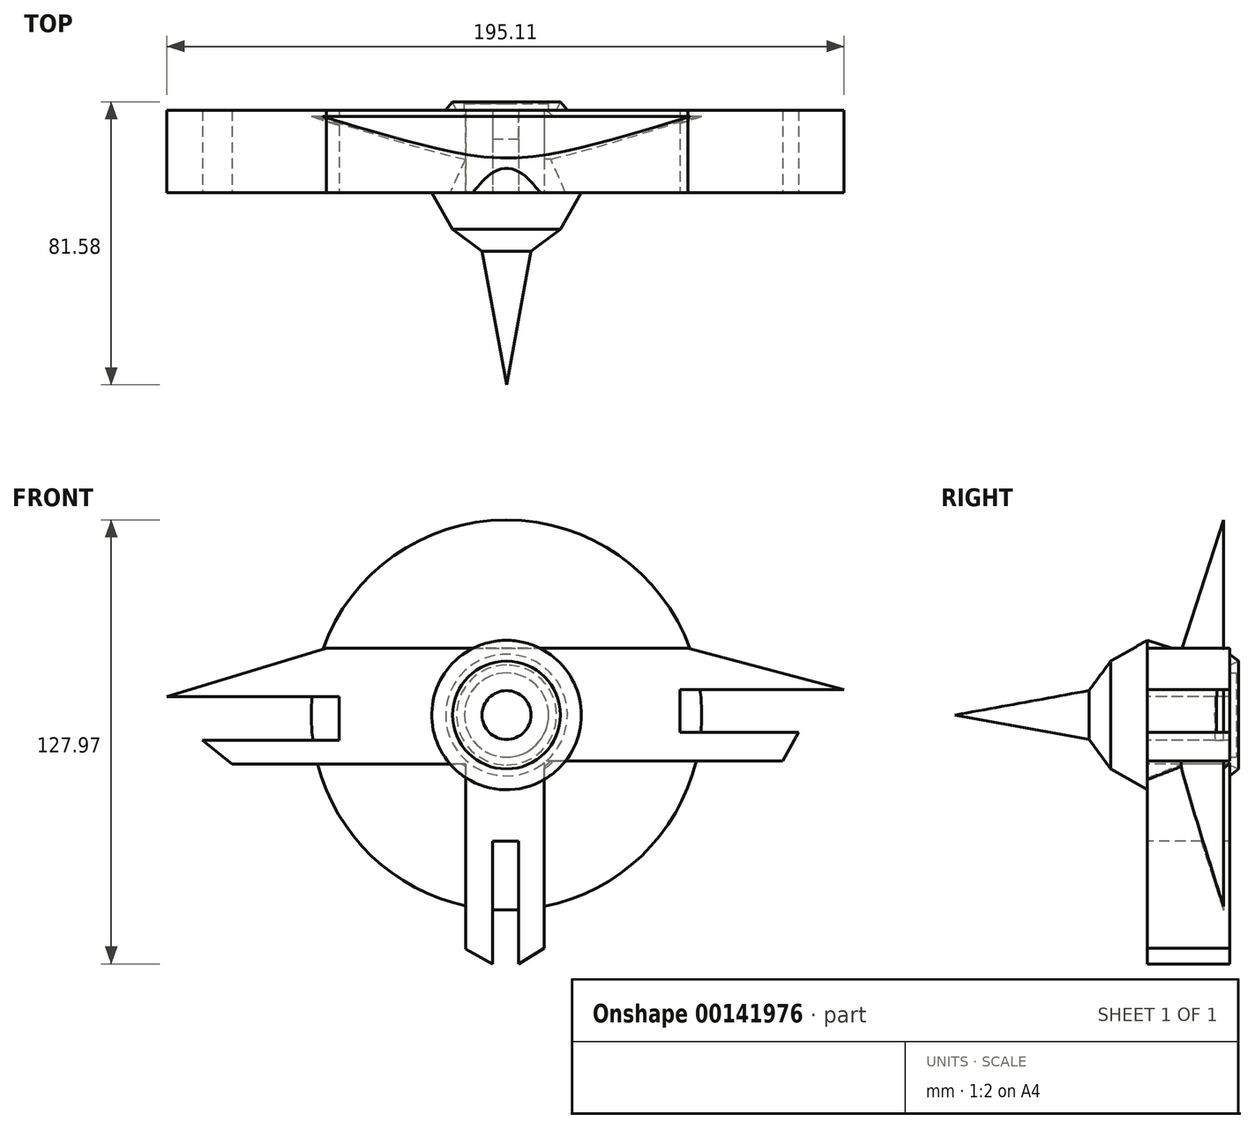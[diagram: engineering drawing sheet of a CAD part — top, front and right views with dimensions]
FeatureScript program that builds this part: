
annotation { "Feature Type Name" : "Feature", "Feature Type Description" : "" }
export const myFeature = defineFeature(function(context is Context, id is Id, definition is map)
    precondition{}
    {
        {
            var Q0;
            Q0=qCreatedBy(makeId("Right.planeOp"),FACE);
            var sketch = newSketch(context, id + "F0", { "sketchPlane" : qUnion([Q0])});
            skLineSegment(sketch, "E0", {"start": v(-55.34, 0) * mm, "end": v(0, -10.13) * mm});
            skLineSegment(sketch, "E1", {"start": v(0, -10.13) * mm, "end": v(-16.84, -7.04) * mm});
            skLineSegment(sketch, "E2", {"start": v(-16.84, -7.04) * mm, "end": v(-10.55, -15.55) * mm});
            skLineSegment(sketch, "E3", {"start": v(-10.55, -15.55) * mm, "end": v(0, -21.54) * mm});
            skLineSegment(sketch, "E4", {"start": v(0, -21.54) * mm, "end": v(9.7, -18.4) * mm});
            skLineSegment(sketch, "E5", {"start": v(9.7, -18.4) * mm, "end": v(21.94, -56.23) * mm});
            skLineSegment(sketch, "E6", {"start": v(21.94, -56.23) * mm, "end": v(21.94, -18.97) * mm});
            skLineSegment(sketch, "E7", {"start": v(21.94, -18.97) * mm, "end": v(26.24, -15.55) * mm});
            skLineSegment(sketch, "E8", {"start": v(26.24, -15.55) * mm, "end": v(18.83, -12.12) * mm});
            skLineSegment(sketch, "E9", {"start": v(18.83, -12.12) * mm, "end": v(25.67, -12.12) * mm});
            skLineSegment(sketch, "E10", {"start": v(25.67, -12.12) * mm, "end": v(25.67, 0) * mm});
            skLineSegment(sketch, "E11", {"start": v(25.67, 0) * mm, "end": v(0, 0) * mm});
            skLineSegment(sketch, "E12", {"start": v(0, 0) * mm, "end": v(-55.34, 0) * mm});
            skSolve(sketch);
        }
        {
            var Q0;
            Q0 = qSketchRegion(id + "F0", true);
            var Q1;
            Q1=sQuery(id+"F0.wireOp",EDGE,"E12");
            revolve(context, id + "F1", {"entities" : qUnion([Q0]), "axis" : qUnion([Q1]), "revolveType" : RevolveType.FULL});
        }
        {
            var Q0;
            Q0=qCreatedBy(makeId("Front.planeOp"),FACE);
            var sketch = newSketch(context, id + "F2", { "sketchPlane" : qUnion([Q0])});
            skLineSegment(sketch, "E13", {"start": v(0, 76.87) * mm, "end": v(0, -76.59) * mm});
            skLineSegment(sketch, "E14", {"start": v(0, -76.59) * mm, "end": v(0, 0) * mm});
            skLineSegment(sketch, "E15", {"start": v(0, 0) * mm, "end": v(-76.44, 0) * mm});
            skLineSegment(sketch, "E16", {"start": v(-76.44, 0) * mm, "end": v(76.16, 0) * mm});
            skLineSegment(sketch, "E17", {"start": v(76.16, 0) * mm, "end": v(49.92, 0) * mm});
            skLineSegment(sketch, "E18", {"start": v(49.92, 0) * mm, "end": v(49.92, 4.7) * mm});
            skLineSegment(sketch, "E19", {"start": v(49.92, 4.7) * mm, "end": v(49.92, -5) * mm});
            skLineSegment(sketch, "E20", {"start": v(49.92, -5) * mm, "end": v(84.15, -5) * mm});
            skLineSegment(sketch, "E21", {"start": v(84.15, -5) * mm, "end": v(79.58, -13.26) * mm});
            skLineSegment(sketch, "E22", {"start": v(79.58, -13.26) * mm, "end": v(10.84, -13.26) * mm});
            skLineSegment(sketch, "E23", {"start": v(10.84, -13.26) * mm, "end": v(10.84, -67.17) * mm});
            skLineSegment(sketch, "E24", {"start": v(10.84, -67.17) * mm, "end": v(3.42, -71.74) * mm});
            skLineSegment(sketch, "E25", {"start": v(3.42, -71.74) * mm, "end": v(3.42, -36.37) * mm});
            skLineSegment(sketch, "E26", {"start": v(3.42, -36.37) * mm, "end": v(-4, -36.37) * mm});
            skLineSegment(sketch, "E27", {"start": v(-4, -36.37) * mm, "end": v(-4, -71.74) * mm});
            skLineSegment(sketch, "E28", {"start": v(-4, -71.74) * mm, "end": v(-11.7, -67.46) * mm});
            skLineSegment(sketch, "E29", {"start": v(-11.7, -67.46) * mm, "end": v(-11.7, -14.12) * mm});
            skLineSegment(sketch, "E30", {"start": v(-11.7, -14.12) * mm, "end": v(-79.01, -14.12) * mm});
            skLineSegment(sketch, "E31", {"start": v(-79.01, -14.12) * mm, "end": v(-87.57, -7.27) * mm});
            skLineSegment(sketch, "E32", {"start": v(-87.57, -7.27) * mm, "end": v(-48.2, -7.27) * mm});
            skLineSegment(sketch, "E33", {"start": v(-48.2, -7.27) * mm, "end": v(-48.2, 5.28) * mm});
            skLineSegment(sketch, "E34", {"start": v(-48.2, 5.28) * mm, "end": v(-97.84, 5.28) * mm});
            skLineSegment(sketch, "E35", {"start": v(-97.84, 5.28) * mm, "end": v(-51.91, 19.25) * mm});
            skLineSegment(sketch, "E36", {"start": v(-51.91, 19.25) * mm, "end": v(52.2, 19.25) * mm});
            skLineSegment(sketch, "E37", {"start": v(52.2, 19.25) * mm, "end": v(97.27, 7.27) * mm});
            skLineSegment(sketch, "E38", {"start": v(97.27, 7.27) * mm, "end": v(49.92, 7.27) * mm});
            skLineSegment(sketch, "E39", {"start": v(49.92, 7.27) * mm, "end": v(49.92, 4.7) * mm});
            skSolve(sketch);
        }
        {
            var Q0;
            Q0 = qSketchRegion(id + "F2", true);
            extrude(context, id + "F3", {"entities" : qUnion([Q0]), "operationType" : NewBodyOperationType.ADD, "oppositeDirection" : true, "depth" : 23.75 * mm});
        }
    });
